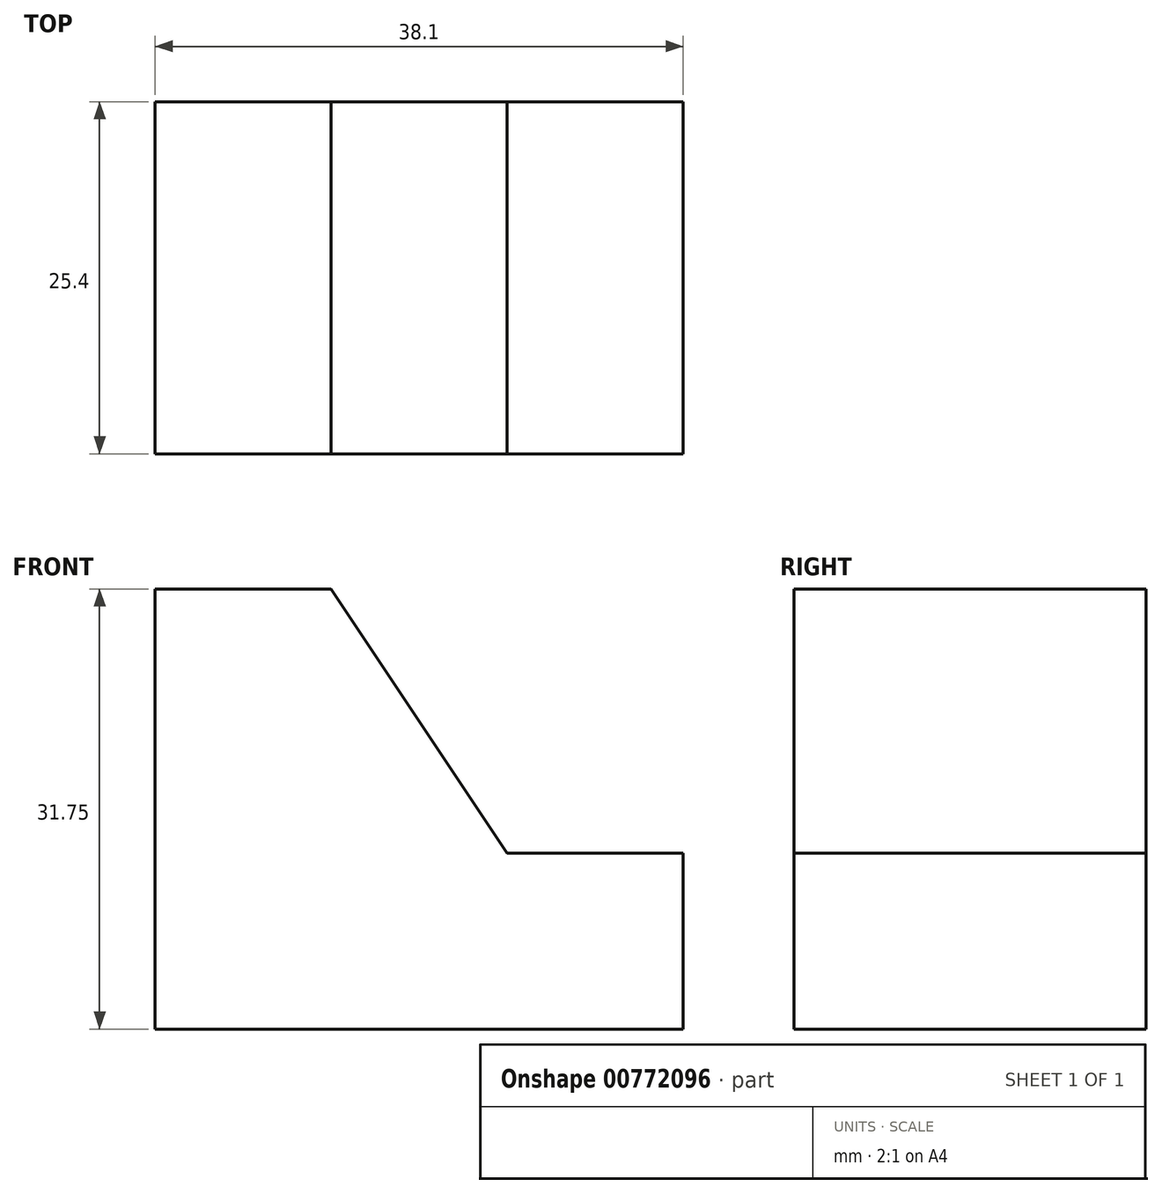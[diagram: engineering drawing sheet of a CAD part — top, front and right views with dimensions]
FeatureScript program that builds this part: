
annotation { "Feature Type Name" : "Feature", "Feature Type Description" : "" }
export const myFeature = defineFeature(function(context is Context, id is Id, definition is map)
    precondition{}
    {
        {
            var Q0;
            Q0=qCreatedBy(makeId("Front.planeOp"),FACE);
            var sketch = newSketch(context, id + "F0", { "sketchPlane" : qUnion([Q0])});
            skLineSegment(sketch, "E0", {"start": v(0, 0) * mm, "end": v(0, 12.7) * mm});
            skLineSegment(sketch, "E1", {"start": v(0, 12.7) * mm, "end": v(-12.7, 12.7) * mm});
            skLineSegment(sketch, "E2", {"start": v(0, 0) * mm, "end": v(-38.1, 0) * mm});
            skLineSegment(sketch, "E3", {"start": v(-38.1, 0) * mm, "end": v(-38.1, 31.75) * mm});
            skLineSegment(sketch, "E4", {"start": v(-38.1, 31.75) * mm, "end": v(-25.4, 31.75) * mm});
            skLineSegment(sketch, "E5", {"start": v(-12.7, 12.7) * mm, "end": v(-25.4, 31.75) * mm});
            skSolve(sketch);
        }
        {
            var Q0;
            Q0 = qSketchRegion(id + "F0", true);
            extrude(context, id + "F1", {"entities" : qUnion([Q0]), "depth" : 25.4 * mm, "offsetDistance" : 25.4 * mm});
        }
    });
